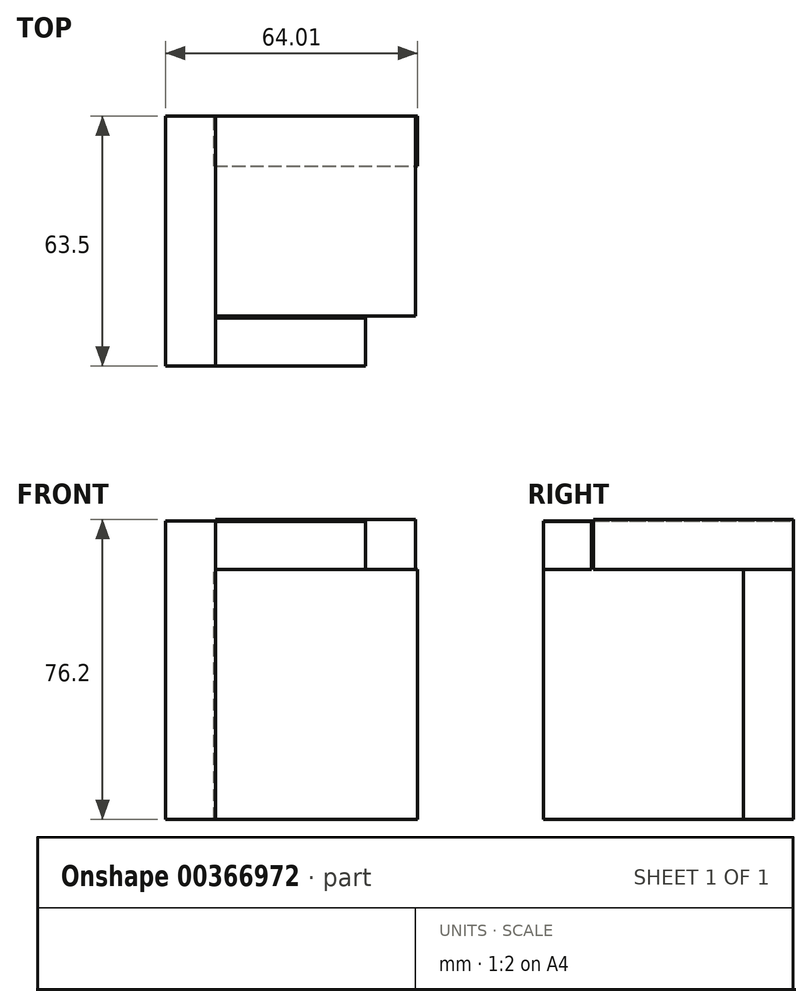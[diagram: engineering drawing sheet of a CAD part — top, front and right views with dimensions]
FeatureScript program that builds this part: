
annotation { "Feature Type Name" : "Feature", "Feature Type Description" : "" }
export const myFeature = defineFeature(function(context is Context, id is Id, definition is map)
    precondition{}
    {
        {
            var Q0;
            Q0=qCreatedBy(makeId("Front.planeOp"),FACE);
            var sketch = newSketch(context, id + "F0", { "sketchPlane" : qUnion([Q0])});
            skLineSegment(sketch, "E0.bottom", {"start": v(0, 0) * mm, "end": v(12.7, 0) * mm});
            skLineSegment(sketch, "E0.top", {"start": v(0, -63.5) * mm, "end": v(12.7, -63.5) * mm});
            skLineSegment(sketch, "E0.left", {"start": v(0, 0) * mm, "end": v(0, -63.5) * mm});
            skLineSegment(sketch, "E0.right", {"start": v(12.7, 0) * mm, "end": v(12.7, -63.5) * mm});
            skSolve(sketch);
        }
        {
            var Q0;
            Q0=qCreatedBy(makeId("Front.planeOp"),FACE);
            var sketch = newSketch(context, id + "F1", { "sketchPlane" : qUnion([Q0])});
            skSolve(sketch);
        }
        {
            var Q0;
            Q0=makeQuery(id+"F0.imprint","IMPRINT",FACE,{"disambiguationData":[TD([[makeQuery(id+"F0.imprint","IMPRINT",EDGE,{"derivedFrom":sQuery(id+"F0.wireOp",EDGE,"E0.bottom")}),-1.0]])]});
            var Q1;
            Q1 = qSketchRegion(id + "F1", true);
            extrude(context, id + "F2", {"entities" : qUnion([Q0, Q1]), "depth" : 63.5 * mm});
        }
        {
            var Q0;
            Q0=qCreatedBy(makeId("Top.planeOp"),FACE);
            var sketch = newSketch(context, id + "F3", { "sketchPlane" : qUnion([Q0])});
            skLineSegment(sketch, "E1.bottom", {"start": v(12.7, 0) * mm, "end": v(63.5, 0) * mm});
            skLineSegment(sketch, "E1.top", {"start": v(12.7, -50.8) * mm, "end": v(63.5, -50.8) * mm});
            skLineSegment(sketch, "E1.left", {"start": v(12.7, 0) * mm, "end": v(12.7, -50.8) * mm});
            skLineSegment(sketch, "E1.right", {"start": v(63.5, 0) * mm, "end": v(63.5, -50.8) * mm});
            skSolve(sketch);
        }
        {
            var Q0;
            Q0=makeQuery(id+"F3.imprint","IMPRINT",FACE,{"disambiguationData":[TD([[makeQuery(id+"F3.imprint","IMPRINT",EDGE,{"derivedFrom":sQuery(id+"F3.wireOp",EDGE,"E1.bottom")}),-1.0]])]});
            extrude(context, id + "F4", {"entities" : qUnion([Q0]), "operationType" : NewBodyOperationType.ADD, "depth" : 12.7 * mm});
        }
        {
            var Q0;
            Q0=qCreatedBy(makeId("Front.planeOp"),FACE);
            var sketch = newSketch(context, id + "F5", { "sketchPlane" : qUnion([Q0])});
            skLineSegment(sketch, "E2.bottom", {"start": v(12.7, 0) * mm, "end": v(0, 0) * mm});
            skLineSegment(sketch, "E2.top", {"start": v(12.7, 12.34) * mm, "end": v(0, 12.34) * mm});
            skLineSegment(sketch, "E2.left", {"start": v(12.7, 0) * mm, "end": v(12.7, 12.34) * mm});
            skLineSegment(sketch, "E2.right", {"start": v(0, 0) * mm, "end": v(0, 12.34) * mm});
            skSolve(sketch);
        }
        {
            var Q0;
            Q0=makeQuery(id+"F5.imprint","IMPRINT",FACE,{"disambiguationData":[TD([[makeQuery(id+"F5.imprint","IMPRINT",EDGE,{"derivedFrom":sQuery(id+"F5.wireOp",EDGE,"E2.bottom")}),-1.0]])]});
            extrude(context, id + "F6", {"entities" : qUnion([Q0]), "operationType" : NewBodyOperationType.ADD, "depth" : 12.7 * mm});
        }
        {
            var Q0;
            Q0=makeQuery(id+"F6.opExtrude","CAP_FACE",FACE,{"disambiguationData":[OSD([sQuery(id+"F5.wireOp",EDGE,"E2.bottom"),sQuery(id+"F5.wireOp",EDGE,"E2.top"),sQuery(id+"F5.wireOp",EDGE,"E2.left"),sQuery(id+"F5.wireOp",EDGE,"E2.right")])],"isStart":false});
            extrude(context, id + "F7", {"entities" : qUnion([Q0]), "operationType" : NewBodyOperationType.ADD, "depth" : 50.8 * mm});
        }
        {
            var Q0;
            Q0=qCreatedBy(makeId("Front.planeOp"),FACE);
            var sketch = newSketch(context, id + "F8", { "sketchPlane" : qUnion([Q0])});
            skLineSegment(sketch, "E3.bottom", {"start": v(12.32, -63.45) * mm, "end": v(64.01, -63.45) * mm});
            skLineSegment(sketch, "E3.top", {"start": v(12.32, 0) * mm, "end": v(64.01, 0) * mm});
            skLineSegment(sketch, "E3.left", {"start": v(12.32, -63.45) * mm, "end": v(12.32, 0) * mm});
            skLineSegment(sketch, "E3.right", {"start": v(64.01, -63.45) * mm, "end": v(64.01, 0) * mm});
            skSolve(sketch);
        }
        {
            var Q0;
            Q0=makeQuery(id+"F8.imprint","IMPRINT",FACE,{"disambiguationData":[TD([[makeQuery(id+"F8.imprint","IMPRINT",EDGE,{"derivedFrom":sQuery(id+"F8.wireOp",EDGE,"E3.bottom")}),1.0]])]});
            extrude(context, id + "F9", {"entities" : qUnion([Q0]), "depth" : 12.7 * mm});
        }
        {
            var Q0;
            Q0=qCreatedBy(makeId("Right.planeOp"),FACE);
            var sketch = newSketch(context, id + "F10", { "sketchPlane" : qUnion([Q0])});
            skLineSegment(sketch, "E4.bottom", {"start": v(-51.27, 0) * mm, "end": v(-63.49, 0) * mm});
            skLineSegment(sketch, "E4.top", {"start": v(-51.27, 12.16) * mm, "end": v(-63.49, 12.16) * mm});
            skLineSegment(sketch, "E4.left", {"start": v(-51.27, 0) * mm, "end": v(-51.27, 12.16) * mm});
            skLineSegment(sketch, "E4.right", {"start": v(-63.49, 0) * mm, "end": v(-63.49, 12.16) * mm});
            skSolve(sketch);
        }
        {
            var Q0;
            Q0=makeQuery(id+"F10.imprint","IMPRINT",FACE,{"disambiguationData":[TD([[makeQuery(id+"F10.imprint","IMPRINT",EDGE,{"derivedFrom":sQuery(id+"F10.wireOp",EDGE,"E4.bottom")}),-1.0]])]});
            extrude(context, id + "F11", {"entities" : qUnion([Q0]), "operationType" : NewBodyOperationType.ADD, "depth" : 38.1 * mm});
        }
        {
            var Q0;
            Q0=makeQuery(id+"F11.opExtrude","CAP_FACE",FACE,{"disambiguationData":[OSD([sQuery(id+"F10.wireOp",EDGE,"E4.bottom"),sQuery(id+"F10.wireOp",EDGE,"E4.top"),sQuery(id+"F10.wireOp",EDGE,"E4.left"),sQuery(id+"F10.wireOp",EDGE,"E4.right")])],"isStart":false});
            extrude(context, id + "F12", {"entities" : qUnion([Q0]), "operationType" : NewBodyOperationType.ADD, "depth" : 12.7 * mm});
        }
    });
